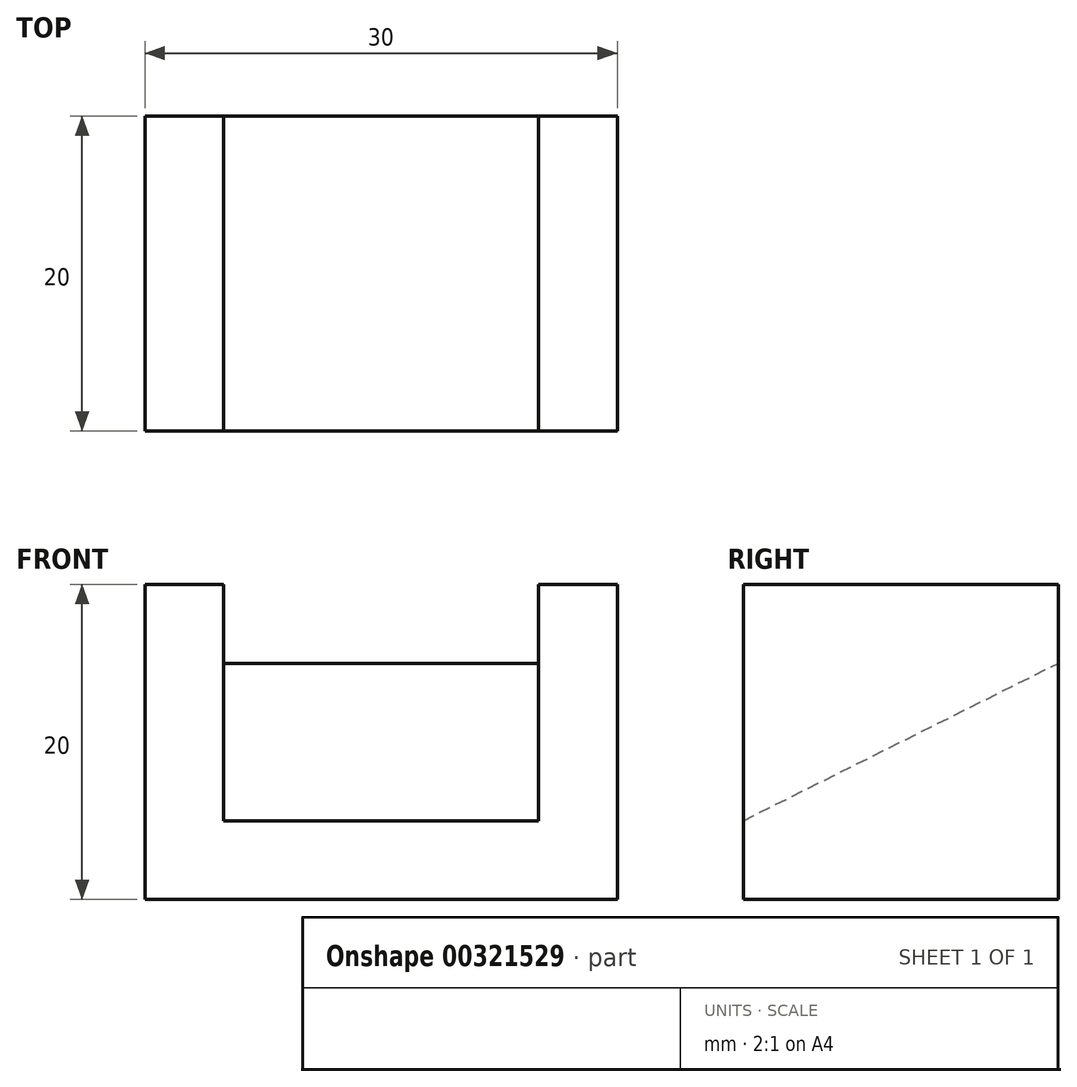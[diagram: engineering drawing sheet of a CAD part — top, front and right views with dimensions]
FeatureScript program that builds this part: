
annotation { "Feature Type Name" : "Feature", "Feature Type Description" : "" }
export const myFeature = defineFeature(function(context is Context, id is Id, definition is map)
    precondition{}
    {
        {
            var Q0;
            Q0=qCreatedBy(makeId("Right.planeOp"),FACE);
            var sketch = newSketch(context, id + "F0", { "sketchPlane" : qUnion([Q0])});
            skLineSegment(sketch, "E0", {"start": v(0, 0) * mm, "end": v(0, 20) * mm});
            skLineSegment(sketch, "E1", {"start": v(0, 20) * mm, "end": v(20, 20) * mm});
            skLineSegment(sketch, "E2", {"start": v(20, 20) * mm, "end": v(20, 0) * mm});
            skLineSegment(sketch, "E3", {"start": v(20, 0) * mm, "end": v(0, 0) * mm});
            skLineSegment(sketch, "E4", {"start": v(0, 5) * mm, "end": v(20, 15) * mm});
            skSolve(sketch);
        }
        {
            var Q0;
            {var subQ0=sQuery(id+"F0.wireOp",EDGE,"E1");Q0=makeQuery(id+"F0.imprint","IMPRINT",FACE,{"disambiguationData":[TD([[makeQuery(id+"F0.imprint","IMPRINT",EDGE,{"derivedFrom":subQ0}),-1.0]])]});}
            var Q1;
            {var subQ0=sQuery(id+"F0.wireOp",EDGE,"E3");Q1=makeQuery(id+"F0.imprint","IMPRINT",FACE,{"disambiguationData":[TD([[makeQuery(id+"F0.imprint","IMPRINT",EDGE,{"derivedFrom":subQ0}),-1.0]])]});}
            extrude(context, id + "F1", {"entities" : qUnion([Q0, Q1]), "endBound" : BoundingType.SYMMETRIC, "depth" : 30 * mm});
        }
        {
            var Q0;
            {var subQ0=sQuery(id+"F0.wireOp",EDGE,"E1");Q0=makeQuery(id+"F0.imprint","IMPRINT",FACE,{"disambiguationData":[TD([[makeQuery(id+"F0.imprint","IMPRINT",EDGE,{"derivedFrom":subQ0}),-1.0]])]});}
            extrude(context, id + "F2", {"entities" : qUnion([Q0]), "operationType" : NewBodyOperationType.REMOVE, "endBound" : BoundingType.SYMMETRIC, "oppositeDirection" : true, "depth" : 20 * mm});
        }
    });
